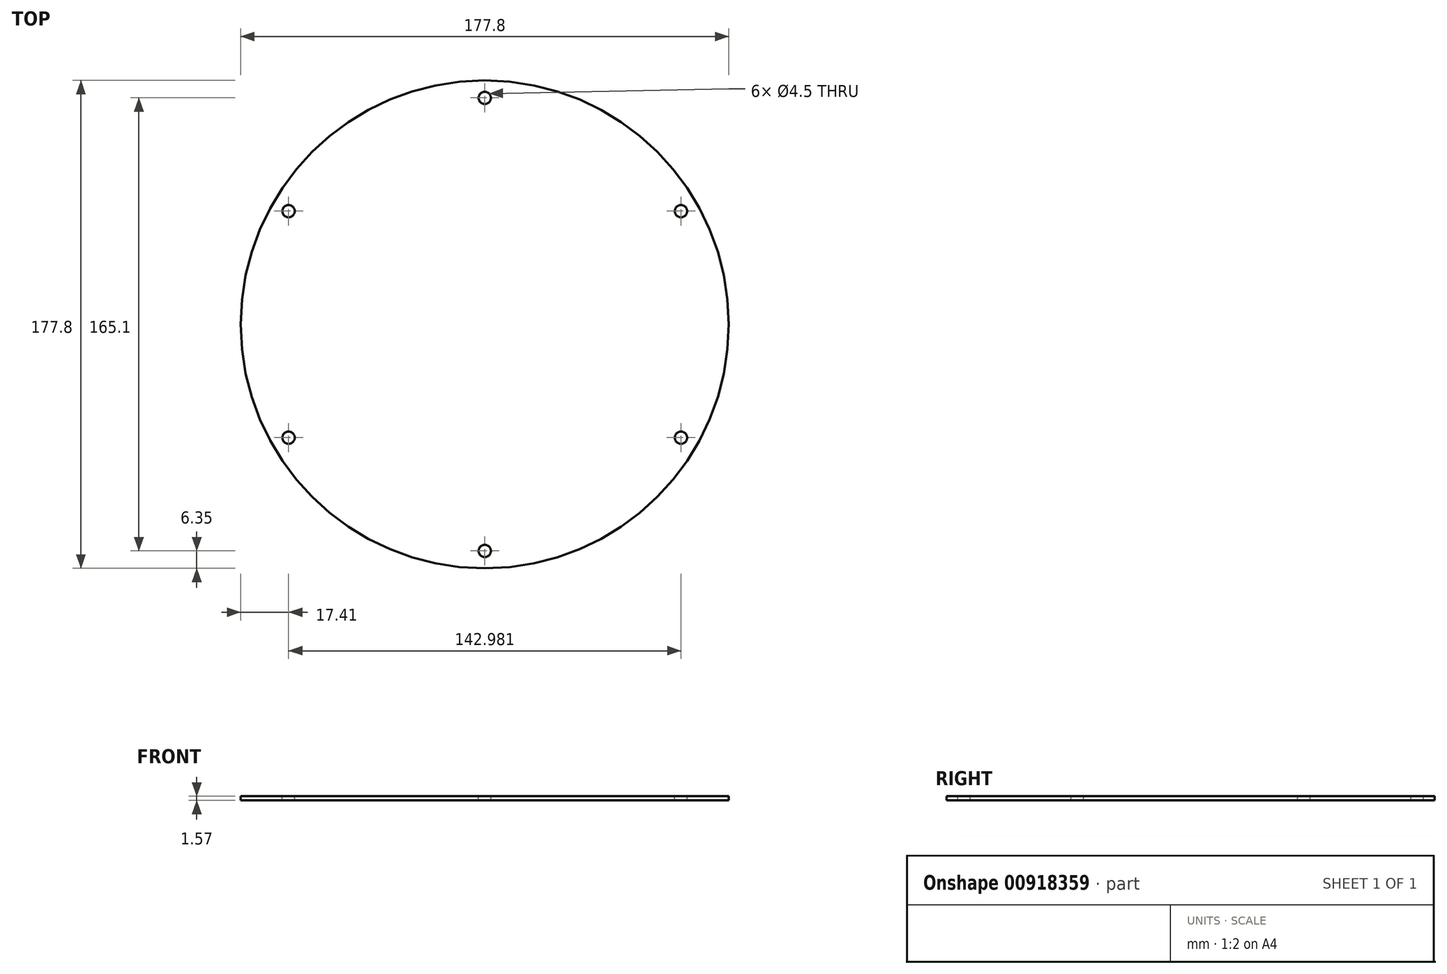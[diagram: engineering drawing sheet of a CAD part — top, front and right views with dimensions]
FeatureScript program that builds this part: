
annotation { "Feature Type Name" : "Feature", "Feature Type Description" : "" }
export const myFeature = defineFeature(function(context is Context, id is Id, definition is map)
    precondition{}
    {
        {
            var Q0;
            Q0=qCreatedBy(makeId("Top.planeOp"),FACE);
            var sketch = newSketch(context, id + "F0", { "sketchPlane" : qUnion([Q0])});
            skCircle(sketch, "E0", {"center": v(0, 0) * mm, "radius": 88.9 * mm});
            skSolve(sketch);
        }
        {
            var Q0;
            Q0 = qSketchRegion(id + "F0", true);
            extrude(context, id + "F1", {"entities" : qUnion([Q0]), "oppositeDirection" : true, "depth" : 1.57 * mm, "offsetDistance" : 25.4 * mm});
        }
        {
            var Q0;
            Q0=makeQuery(id+"F1.opExtrude","CAP_FACE",FACE,{"disambiguationData":[OSD([sQuery(id+"F0.wireOp",EDGE,"E0")])],"isStart":true});
            var sketch = newSketch(context, id + "F2", { "sketchPlane" : qUnion([Q0])});
            skPoint(sketch, "E1", {"position": v(0, 82.55) * mm});
            skPoint(sketch, "E2.1.0", {"position": v(71.5, -41.28) * mm});
            skPoint(sketch, "E2.2.0", {"position": v(-71.5, -41.27) * mm});
            skPoint(sketch, "E2.center", {"position": v(0, 0) * mm});
            skLineSegment(sketch, "E2.anchor1", {"start": v(0, 0) * mm, "end": v(0, 82.55) * mm, "construction": true});
            skLineSegment(sketch, "E2.anchor2", {"start": v(0, 0) * mm, "end": v(-71.5, -41.27) * mm, "construction": true});
            skSolve(sketch);
        }
        {
            var Q0;
            Q0=sQuery(id+"F2.wireOp",VERTEX,"E2.anchor1.end");
            var Q1;
            Q1=sQuery(id+"F2.wireOp",VERTEX,"E2.2.0");
            var Q2;
            Q2=sQuery(id+"F2.wireOp",VERTEX,"E2.1.0");
            var Q3;
            Q3=makeQuery(id+"F1.opExtrude","SWEPT_BODY",BODY,{"disambiguationData":[OSD([sQuery(id+"F0.wireOp",EDGE,"E0")])]});
            hole(context, id + "F3", {"style" : HoleStyle.SIMPLE, "endStyle" : HoleEndStyle.THROUGH, "holeDiameter" : 4.5 * mm, "majorDiameter" : 6.35 * mm, "isTappedThrough" : true, "tappedDepth" : 12.7 * mm, "tapClearance" : 3, "locations" : qUnion([Q0, Q1, Q2]), "scope" : qUnion([Q3])});
        }
        {
            var Q0;
            Q0=makeQuery(id+"F1.opExtrude","CAP_FACE",FACE,{"disambiguationData":[OSD([sQuery(id+"F0.wireOp",EDGE,"E0")])],"isStart":true});
            var sketch = newSketch(context, id + "F4", { "sketchPlane" : qUnion([Q0])});
            skPoint(sketch, "E3", {"position": v(0, -82.55) * mm});
            skPoint(sketch, "E4.1.0", {"position": v(71.5, 41.27) * mm});
            skPoint(sketch, "E4.2.0", {"position": v(-71.5, 41.28) * mm});
            skPoint(sketch, "E4.center", {"position": v(0, 0) * mm});
            skSolve(sketch);
        }
        {
            var Q0;
            Q0=sQuery(id+"F4.wireOp",VERTEX,"E3");
            var Q1;
            Q1=sQuery(id+"F4.wireOp",VERTEX,"E4.1.0");
            var Q2;
            Q2=sQuery(id+"F4.wireOp",VERTEX,"E4.2.0");
            var Q3;
            Q3=makeQuery(id+"F1.opExtrude","SWEPT_BODY",BODY,{"disambiguationData":[OSD([sQuery(id+"F0.wireOp",EDGE,"E0")])]});
            hole(context, id + "F5", {"style" : HoleStyle.SIMPLE, "endStyle" : HoleEndStyle.THROUGH, "holeDiameter" : 4.5 * mm, "majorDiameter" : 6.35 * mm, "isTappedThrough" : true, "tappedDepth" : 12.7 * mm, "tapClearance" : 3, "locations" : qUnion([Q0, Q1, Q2]), "scope" : qUnion([Q3])});
        }
    });
